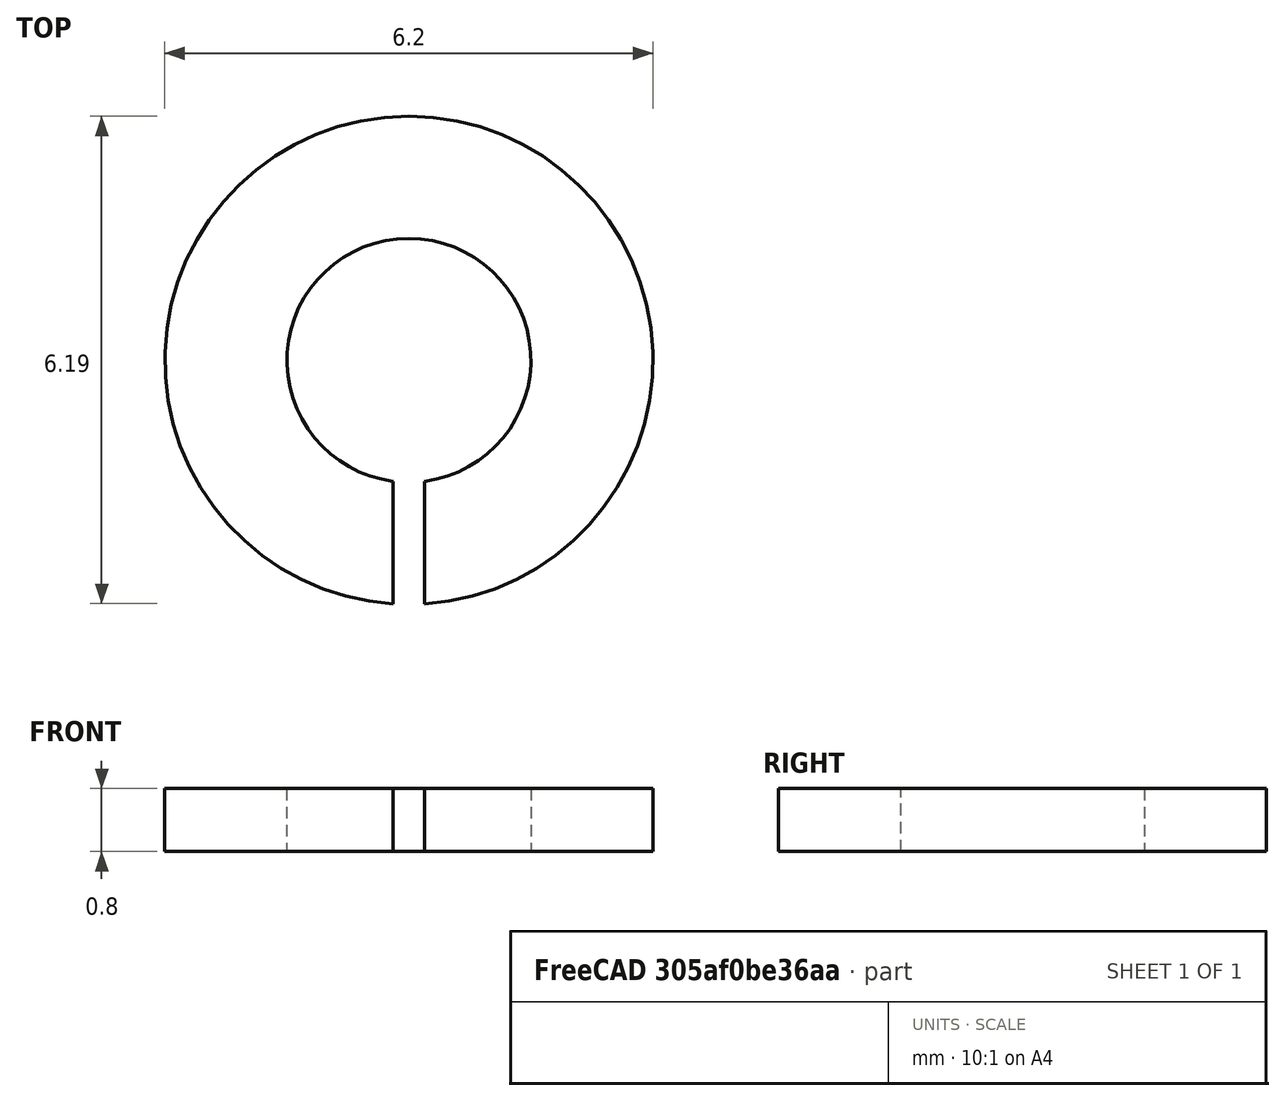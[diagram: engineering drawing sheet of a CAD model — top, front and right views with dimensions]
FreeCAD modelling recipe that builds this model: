
FCSTD DOCUMENT  (FreeCAD 0.15R4651 (Git))
Label: Federring_DIN127-A3
License: All rights reserved
LicenseURL: http://de.wikipedia.org/wiki/Alle_Rechte_vorbehalten
objects: Sketcher::SketchObject×1, PartDesign::Pad×1
note: 3 computed .brp shape members not serialized (recipe doc carries the construction recipe); baked Part::Feature solids carry a one-line shape summary decoded from their .brp

FEATURE [Sketcher::SketchObject] Sketch
  sketch-geometry (4):
    g0: ArcOfCircle CenterX=0 CenterY=0 CenterZ=0 NormalX=0 NormalY=0 NormalZ=1 Radius=1.55 StartAngle=4.84178 EndAngle=10.8662
    g1: ArcOfCircle CenterX=0 CenterY=0 CenterZ=0 NormalX=0 NormalY=0 NormalZ=1 Radius=3.1 StartAngle=4.77695 EndAngle=10.931
    g2: LineSegment StartX=0.2 StartY=-1.53704 StartZ=0 EndX=0.2 EndY=-3.09354 EndZ=0
    g3: LineSegment StartX=-0.2 StartY=-3.09354 StartZ=0 EndX=-0.2 EndY=-1.53704 EndZ=0
  constraints (12):
    c: Coincident(g0,g-1)
    c: Coincident(g1,g-1)
    c: Vertical(g2)
    c: Vertical(g3)
    c: Coincident(g0,g2)
    c: Coincident(g0,g3)
    c: Coincident(g1,g2)
    c: Coincident(g1,g3)
    c: Symmetric(g1,g1,g-2)
    c: Radius(g0) = 1.55
    c: Radius(g1) = 3.1
    c: DistanceX(g1,g1) = -0.4
FEATURE [PartDesign::Pad] Pad  label="Federring DIN 127-A 3 #"
  Length = 0.8
  Length2 = 100
  Midplane = true
  Sketch = -> Sketch
  Type = 0
